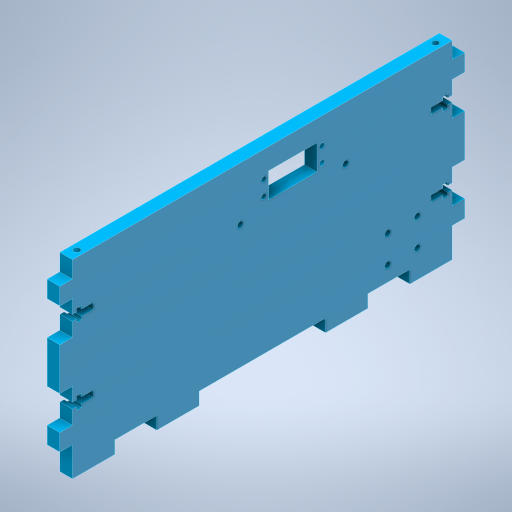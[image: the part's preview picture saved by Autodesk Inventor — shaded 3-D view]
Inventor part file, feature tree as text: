
AUTODESK INVENTOR PART (.ipt)
format: ipt  version: 2024.2 (Build 282272000, 272)  size: 491,520 bytes
history: native  units: mm
features: other x7, extrude x6, sketch x6, reference x2, projected_geometry x1
ambient origin geometry x8: Origin, YZ Plane, XZ Plane, XY Plane, X Axis, Y Axis, Z Axis, Center Point
bodies: Body1 (feature_tree)
feature tree (22):
  other  "Твердое тело1"
  extrude  "Выдавливание1"  Depth=180.0mm
  extrude  "Выдавливание4"  Depth=84.0mm
  extrude  "Выдавливание5"  Depth=90.0mm
  extrude  "Выдавливание7"  TaperAngle=0.0deg  [1 undecoded]
  extrude  "Выдавливание8"  Depth=6.0mm
  extrude  "Выдавливание9"  Depth=8.0mm
  sketch  "Эскиз1"
  sketch  "Эскиз4"
  sketch  "Эскиз6"
  sketch  "Эскиз8"
  sketch  "Эскиз9"
  reference  "Ссылка1"
  reference  "Ссылка2"
  sketch  "Эскиз10"
  projected_geometry  "Спроецированная петля1"
  other  "<userpath>\Documents\Artist\3D\Робот.iam"
  other  "Робот.iam"
  other  "каретка:1"
  other  "ANY:13"
  other  "Проецирование ребер1"
  other  "Проецирование ребер2"
note: 1 required parameter value undecoded (feature->parameter linkage not recoverable at this tier; creation-order binding heuristic only, values carry confidence <= 0.55)
